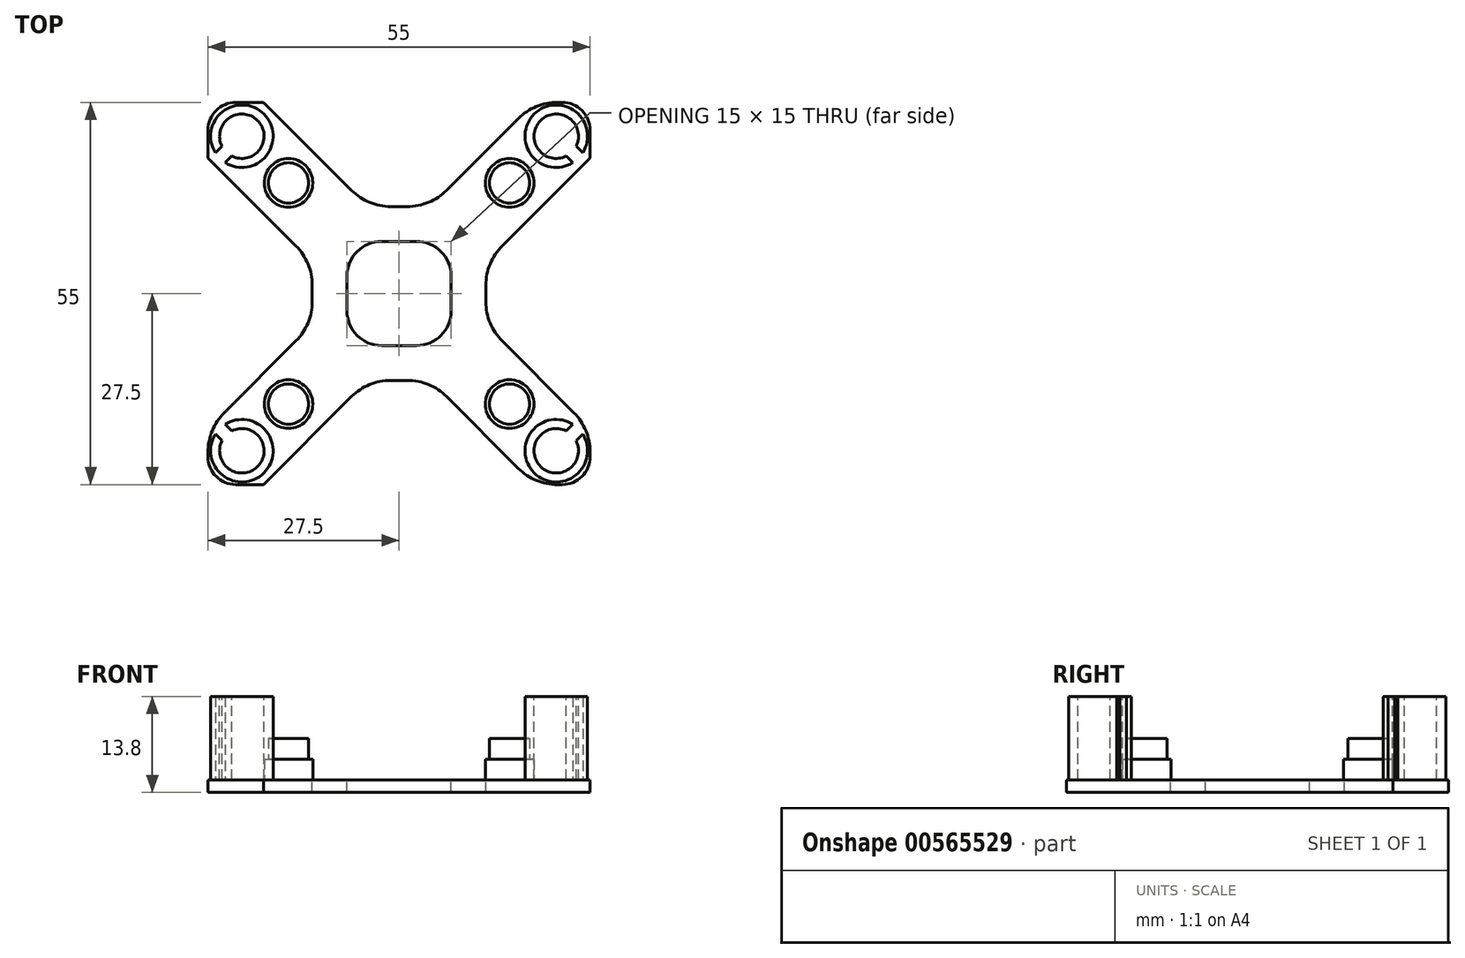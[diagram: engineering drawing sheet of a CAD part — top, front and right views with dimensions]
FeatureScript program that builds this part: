
annotation { "Feature Type Name" : "Feature", "Feature Type Description" : "" }
export const myFeature = defineFeature(function(context is Context, id is Id, definition is map)
    precondition{}
    {
        {
            var Q0;
            Q0=qCreatedBy(makeId("Top.planeOp"),FACE);
            var sketch = newSketch(context, id + "F0", { "sketchPlane" : qUnion([Q0])});
            skLineSegment(sketch, "E0.bottom", {"start": v(-27.5, 27.5) * mm, "end": v(27.5, 27.5) * mm});
            skLineSegment(sketch, "E0.top", {"start": v(-27.5, -27.5) * mm, "end": v(27.5, -27.5) * mm});
            skLineSegment(sketch, "E0.left", {"start": v(-27.5, 27.5) * mm, "end": v(-27.5, -27.5) * mm});
            skLineSegment(sketch, "E0.right", {"start": v(27.5, 27.5) * mm, "end": v(27.5, -27.5) * mm});
            skPoint(sketch, "E0.middle", {"position": v(0, 0) * mm});
            skLineSegment(sketch, "E1", {"start": v(-27.5, 27.5) * mm, "end": v(27.5, -27.5) * mm, "construction": true});
            skLineSegment(sketch, "E2", {"start": v(27.5, 27.5) * mm, "end": v(-27.5, -27.5) * mm, "construction": true});
            skSolve(sketch);
        }
        {
            var Q0;
            Q0=qSketchRegion(id+"F0",true);
            extrude(context, id + "F1", {"entities" : qUnion([Q0]), "depth" : 1.8 * mm, "offsetDistance" : 25 * mm});
        }
        {
            var Q0;
            Q0=makeQuery(id+"F1.opExtrude","CAP_FACE",FACE,{"disambiguationData":[OSD([sQuery(id+"F0.wireOp",EDGE,"E0.bottom"),sQuery(id+"F0.wireOp",EDGE,"E0.top"),sQuery(id+"F0.wireOp",EDGE,"E0.left"),sQuery(id+"F0.wireOp",EDGE,"E0.right")])],"isStart":false});
            var sketch = newSketch(context, id + "F2", { "sketchPlane" : qUnion([Q0])});
            skLineSegment(sketch, "E3", {"start": v(-27.5, 27.5) * mm, "end": v(27.5, -27.5) * mm, "construction": true});
            skLineSegment(sketch, "E4", {"start": v(27.5, 27.5) * mm, "end": v(-27.5, -27.5) * mm, "construction": true});
            skCircle(sketch, "E5", {"center": v(-15.9, 15.9) * mm, "radius": 3.5 * mm});
            skCircle(sketch, "E6", {"center": v(15.9, 15.9) * mm, "radius": 3.5 * mm});
            skCircle(sketch, "E7", {"center": v(-15.9, -15.9) * mm, "radius": 3.5 * mm});
            skCircle(sketch, "E8", {"center": v(15.9, -15.9) * mm, "radius": 3.5 * mm});
            skSolve(sketch);
        }
        {
            var Q0;
            Q0=qSketchRegion(id+"F2",true);
            extrude(context, id + "F3", {"entities" : qUnion([Q0]), "operationType" : NewBodyOperationType.ADD, "depth" : 3 * mm, "offsetDistance" : 25 * mm});
        }
        {
            var Q0;
            Q0=makeQuery(id+"F3.opExtrude","CAP_FACE",FACE,{"disambiguationData":[OSD([sQuery(id+"F2.wireOp",EDGE,"E5")])],"isStart":false});
            var sketch = newSketch(context, id + "F4", { "sketchPlane" : qUnion([Q0])});
            skCircle(sketch, "E9", {"center": v(-15.9, 15.9) * mm, "radius": 2.9 * mm});
            skCircle(sketch, "E10", {"center": v(15.9, 15.9) * mm, "radius": 2.9 * mm});
            skCircle(sketch, "E11", {"center": v(-15.9, -15.9) * mm, "radius": 2.9 * mm});
            skCircle(sketch, "E12", {"center": v(15.9, -15.9) * mm, "radius": 2.9 * mm});
            skSolve(sketch);
        }
        {
            var Q0;
            Q0=qSketchRegion(id+"F4",true);
            extrude(context, id + "F5", {"entities" : qUnion([Q0]), "operationType" : NewBodyOperationType.ADD, "depth" : 3 * mm, "offsetDistance" : 25 * mm});
        }
        {
            var Q0;
            Q0=makeQuery(id+"F1.opExtrude","CAP_FACE",FACE,{"disambiguationData":[OSD([sQuery(id+"F0.wireOp",EDGE,"E0.bottom"),sQuery(id+"F0.wireOp",EDGE,"E0.top"),sQuery(id+"F0.wireOp",EDGE,"E0.left"),sQuery(id+"F0.wireOp",EDGE,"E0.right")])],"isStart":false});
            var sketch = newSketch(context, id + "F6", { "sketchPlane" : qUnion([Q0])});
            skLineSegment(sketch, "E13", {"start": v(-27.5, 27.5) * mm, "end": v(27.5, -27.5) * mm, "construction": true});
            skLineSegment(sketch, "E14", {"start": v(27.5, 27.5) * mm, "end": v(-27.5, -27.5) * mm, "construction": true});
            skCircle(sketch, "E15", {"center": v(-22.63, 22.63) * mm, "radius": 4.5 * mm});
            skCircle(sketch, "E16", {"center": v(22.63, 22.63) * mm, "radius": 4.5 * mm});
            skCircle(sketch, "E17", {"center": v(22.63, -22.63) * mm, "radius": 4.5 * mm});
            skCircle(sketch, "E18", {"center": v(-22.63, -22.63) * mm, "radius": 4.5 * mm});
            skSolve(sketch);
        }
        {
            var Q0;
            Q0=qSketchRegion(id+"F6",true);
            extrude(context, id + "F7", {"entities" : qUnion([Q0]), "operationType" : NewBodyOperationType.ADD, "depth" : 12 * mm, "offsetDistance" : 25 * mm});
        }
        {
            var Q0;
            Q0=makeQuery(id+"F7.opExtrude","CAP_FACE",FACE,{"disambiguationData":[OSD([sQuery(id+"F6.wireOp",EDGE,"E18")])],"isStart":false});
            var sketch = newSketch(context, id + "F8", { "sketchPlane" : qUnion([Q0])});
            skCircle(sketch, "E19", {"center": v(-22.63, -22.63) * mm, "radius": 3.2 * mm});
            skCircle(sketch, "E20", {"center": v(22.63, -22.63) * mm, "radius": 3.2 * mm});
            skCircle(sketch, "E21", {"center": v(-22.63, 22.63) * mm, "radius": 3.2 * mm});
            skCircle(sketch, "E22", {"center": v(22.63, 22.63) * mm, "radius": 3.2 * mm});
            skSolve(sketch);
        }
        {
            var Q0;
            Q0=qSketchRegion(id+"F8",true);
            extrude(context, id + "F9", {"entities" : qUnion([Q0]), "operationType" : NewBodyOperationType.REMOVE, "oppositeDirection" : true, "depth" : 12 * mm, "offsetDistance" : 25 * mm});
        }
        {
            var Q0;
            Q0=makeQuery(id+"F1.opExtrude","SWEPT_EDGE",EDGE,{"disambiguationData":[OSD([sQuery(id+"F0.wireOp",EDGE,"E0.top"),sQuery(id+"F0.wireOp",EDGE,"E0.right")])]});
            var Q1;
            Q1=makeQuery(id+"F1.opExtrude","SWEPT_EDGE",EDGE,{"disambiguationData":[OSD([sQuery(id+"F0.wireOp",EDGE,"E0.top"),sQuery(id+"F0.wireOp",EDGE,"E0.left")])]});
            var Q2;
            Q2=makeQuery(id+"F1.opExtrude","SWEPT_EDGE",EDGE,{"disambiguationData":[OSD([sQuery(id+"F0.wireOp",EDGE,"E0.bottom"),sQuery(id+"F0.wireOp",EDGE,"E0.left")])]});
            var Q3;
            Q3=makeQuery(id+"F1.opExtrude","SWEPT_EDGE",EDGE,{"disambiguationData":[OSD([sQuery(id+"F0.wireOp",EDGE,"E0.bottom"),sQuery(id+"F0.wireOp",EDGE,"E0.right")])]});
            fillet(context, id + "F10", {"entities" : qUnion([Q0, Q1, Q2, Q3]), "radius" : 4 * mm, "tangentPropagation" : true, "allowEdgeOverflow" : false});
        }
        {
            var Q0;
            Q0=makeQuery(id+"F1.opExtrude","CAP_FACE",FACE,{"disambiguationData":[OSD([sQuery(id+"F0.wireOp",EDGE,"E0.bottom"),sQuery(id+"F0.wireOp",EDGE,"E0.top"),sQuery(id+"F0.wireOp",EDGE,"E0.left"),sQuery(id+"F0.wireOp",EDGE,"E0.right")])],"isStart":false});
            var sketch = newSketch(context, id + "F11", { "sketchPlane" : qUnion([Q0])});
            skLineSegment(sketch, "E23.0", {"start": v(-27.5, 27.5) * mm, "end": v(27.5, -27.5) * mm, "construction": true});
            skLineSegment(sketch, "E24.0", {"start": v(27.5, 27.5) * mm, "end": v(-27.5, -27.5) * mm, "construction": true});
            skPoint(sketch, "E25.middle", {"position": v(0, 0) * mm});
            skLineSegment(sketch, "E26", {"start": v(-12.5, 12.5) * mm, "end": v(12.5, 12.5) * mm, "construction": true});
            skLineSegment(sketch, "E27", {"start": v(-12.5, 12.5) * mm, "end": v(-12.5, -12.5) * mm, "construction": true});
            skLineSegment(sketch, "E28", {"start": v(-12.5, -12.5) * mm, "end": v(12.5, -12.5) * mm, "construction": true});
            skLineSegment(sketch, "E29", {"start": v(12.5, -12.5) * mm, "end": v(12.5, 12.5) * mm, "construction": true});
            skLineSegment(sketch, "E30", {"start": v(-27.5, 19.5) * mm, "end": v(-12.5, 4.5) * mm});
            skLineSegment(sketch, "E31", {"start": v(-12.5, 4.5) * mm, "end": v(-12.5, -4.5) * mm});
            skLineSegment(sketch, "E32", {"start": v(-12.5, -4.5) * mm, "end": v(-27.5, -19.5) * mm});
            skLineSegment(sketch, "E33", {"start": v(-27.5, -19.5) * mm, "end": v(-27.5, 19.5) * mm});
            skLineSegment(sketch, "E34", {"start": v(-19.5, 27.5) * mm, "end": v(-4.5, 12.5) * mm});
            skLineSegment(sketch, "E35", {"start": v(-4.5, 12.5) * mm, "end": v(4.5, 12.5) * mm});
            skLineSegment(sketch, "E36", {"start": v(4.5, 12.5) * mm, "end": v(19.5, 27.5) * mm});
            skLineSegment(sketch, "E37", {"start": v(19.5, 27.5) * mm, "end": v(-19.5, 27.5) * mm});
            skLineSegment(sketch, "E38", {"start": v(27.5, 19.5) * mm, "end": v(12.5, 4.5) * mm});
            skLineSegment(sketch, "E39", {"start": v(12.5, 4.5) * mm, "end": v(12.5, -4.5) * mm});
            skLineSegment(sketch, "E40", {"start": v(12.5, -4.5) * mm, "end": v(27.5, -19.5) * mm});
            skLineSegment(sketch, "E41", {"start": v(27.5, -19.5) * mm, "end": v(27.5, 19.5) * mm});
            skLineSegment(sketch, "E42", {"start": v(-19.5, -27.5) * mm, "end": v(-4.5, -12.5) * mm});
            skLineSegment(sketch, "E43", {"start": v(-4.5, -12.5) * mm, "end": v(4.5, -12.5) * mm});
            skLineSegment(sketch, "E44", {"start": v(4.5, -12.5) * mm, "end": v(19.5, -27.5) * mm});
            skLineSegment(sketch, "E45", {"start": v(19.5, -27.5) * mm, "end": v(-19.5, -27.5) * mm});
            skLineSegment(sketch, "E46.bottom", {"start": v(7.5, -7.5) * mm, "end": v(-7.5, -7.5) * mm});
            skLineSegment(sketch, "E46.top", {"start": v(7.5, 7.5) * mm, "end": v(-7.5, 7.5) * mm});
            skLineSegment(sketch, "E46.left", {"start": v(7.5, -7.5) * mm, "end": v(7.5, 7.5) * mm});
            skLineSegment(sketch, "E46.right", {"start": v(-7.5, -7.5) * mm, "end": v(-7.5, 7.5) * mm});
            skSolve(sketch);
        }
        {
            var Q0;
            Q0=qSketchRegion(id+"F11",true);
            extrude(context, id + "F12", {"entities" : qUnion([Q0]), "operationType" : NewBodyOperationType.REMOVE, "endBound" : BoundingType.SYMMETRIC, "oppositeDirection" : true, "depth" : 40 * mm, "offsetDistance" : 25 * mm});
        }
        {
            var Q0;
            Q0=makeQuery(id+"F1.opExtrude","CAP_FACE",FACE,{"disambiguationData":[OSD([sQuery(id+"F0.wireOp",EDGE,"E0.bottom"),sQuery(id+"F0.wireOp",EDGE,"E0.top"),sQuery(id+"F0.wireOp",EDGE,"E0.left"),sQuery(id+"F0.wireOp",EDGE,"E0.right")])],"isStart":false});
            var sketch = newSketch(context, id + "F13", { "sketchPlane" : qUnion([Q0])});
            skLineSegment(sketch, "E47", {"start": v(-14.9, 30.35) * mm, "end": v(-30.28, 14.98) * mm, "construction": true});
            skLineSegment(sketch, "E48", {"start": v(-22.63, 22.63) * mm, "end": v(22.63, 22.63) * mm, "construction": true});
            skPoint(sketch, "E49.cornerSnap0", {"position": v(-27.5, 21.5) * mm});
            skLineSegment(sketch, "E50", {"start": v(-25.43, 18.4) * mm, "end": v(-22.6, 21.24) * mm});
            skLineSegment(sketch, "E51", {"start": v(-22.6, 21.24) * mm, "end": v(-24.02, 22.65) * mm});
            skLineSegment(sketch, "E52", {"start": v(-24.02, 22.65) * mm, "end": v(-26.85, 19.82) * mm});
            skLineSegment(sketch, "E53", {"start": v(-26.85, 19.82) * mm, "end": v(-25.43, 18.4) * mm});
            skLineSegment(sketch, "E54.MirrorCS", {"start": v(25.43, 18.4) * mm, "end": v(22.6, 21.24) * mm});
            skLineSegment(sketch, "E55.MirrorCS", {"start": v(26.85, 19.82) * mm, "end": v(25.43, 18.4) * mm});
            skLineSegment(sketch, "E56.MirrorCS", {"start": v(22.6, 21.24) * mm, "end": v(24.02, 22.65) * mm});
            skLineSegment(sketch, "E57.MirrorCS", {"start": v(24.02, 22.65) * mm, "end": v(26.85, 19.82) * mm});
            skLineSegment(sketch, "E58.MirrorCS", {"start": v(-26.85, -19.82) * mm, "end": v(-25.43, -18.4) * mm});
            skLineSegment(sketch, "E59.MirrorCS", {"start": v(-24.02, -22.65) * mm, "end": v(-26.85, -19.82) * mm});
            skLineSegment(sketch, "E60.MirrorCS", {"start": v(-22.6, -21.24) * mm, "end": v(-24.02, -22.65) * mm});
            skLineSegment(sketch, "E61.MirrorCS", {"start": v(-25.43, -18.4) * mm, "end": v(-22.6, -21.24) * mm});
            skLineSegment(sketch, "E62.MirrorCS", {"start": v(25.43, -18.4) * mm, "end": v(22.6, -21.24) * mm});
            skLineSegment(sketch, "E63.MirrorCS", {"start": v(24.02, -22.65) * mm, "end": v(26.85, -19.82) * mm});
            skLineSegment(sketch, "E64.MirrorCS", {"start": v(26.85, -19.82) * mm, "end": v(25.43, -18.4) * mm});
            skLineSegment(sketch, "E65.MirrorCS", {"start": v(22.6, -21.24) * mm, "end": v(24.02, -22.65) * mm});
            skSolve(sketch);
        }
        {
            var Q0;
            Q0=qSketchRegion(id+"F13",true);
            extrude(context, id + "F14", {"entities" : qUnion([Q0]), "operationType" : NewBodyOperationType.REMOVE, "depth" : 25 * mm, "offsetDistance" : 25 * mm});
        }
        {
            var Q0;
            Q0=makeQuery(id+"F12.boolean.opBoolean","COPY",EDGE,{"derivedFrom":makeQuery(id+"F12.opExtrude","SWEPT_EDGE",EDGE,{"disambiguationData":[OSD([sQuery(id+"F0.wireOp",EDGE,"E0.top"),sQuery(id+"F11.wireOp",EDGE,"E44"),sQuery(id+"F11.wireOp",EDGE,"E45")])]})});
            var Q1;
            Q1=makeQuery(id+"F12.boolean.opBoolean","COPY",EDGE,{"derivedFrom":makeQuery(id+"F12.opExtrude","SWEPT_EDGE",EDGE,{"disambiguationData":[OSD([sQuery(id+"F11.wireOp",EDGE,"E43"),sQuery(id+"F11.wireOp",EDGE,"E44")])]})});
            var Q2;
            Q2=makeQuery(id+"F12.boolean.opBoolean","COPY",EDGE,{"derivedFrom":makeQuery(id+"F12.opExtrude","SWEPT_EDGE",EDGE,{"disambiguationData":[OSD([sQuery(id+"F11.wireOp",EDGE,"E42"),sQuery(id+"F11.wireOp",EDGE,"E43")])]})});
            var Q3;
            Q3=makeQuery(id+"F12.boolean.opBoolean","COPY",EDGE,{"derivedFrom":makeQuery(id+"F12.opExtrude","SWEPT_EDGE",EDGE,{"disambiguationData":[OSD([sQuery(id+"F0.wireOp",EDGE,"E0.top"),sQuery(id+"F11.wireOp",EDGE,"E42"),sQuery(id+"F11.wireOp",EDGE,"E45")])]})});
            var Q4;
            Q4=makeQuery(id+"F12.boolean.opBoolean","COPY",EDGE,{"derivedFrom":makeQuery(id+"F12.opExtrude","SWEPT_EDGE",EDGE,{"disambiguationData":[OSD([sQuery(id+"F0.wireOp",EDGE,"E0.left"),sQuery(id+"F11.wireOp",EDGE,"E32"),sQuery(id+"F11.wireOp",EDGE,"E33")])]})});
            var Q5;
            Q5=makeQuery(id+"F12.boolean.opBoolean","COPY",EDGE,{"derivedFrom":makeQuery(id+"F12.opExtrude","SWEPT_EDGE",EDGE,{"disambiguationData":[OSD([sQuery(id+"F11.wireOp",EDGE,"E31"),sQuery(id+"F11.wireOp",EDGE,"E32")])]})});
            var Q6;
            Q6=makeQuery(id+"F12.boolean.opBoolean","COPY",EDGE,{"derivedFrom":makeQuery(id+"F12.opExtrude","SWEPT_EDGE",EDGE,{"disambiguationData":[OSD([sQuery(id+"F11.wireOp",EDGE,"E30"),sQuery(id+"F11.wireOp",EDGE,"E31")])]})});
            var Q7;
            Q7=makeQuery(id+"F12.boolean.opBoolean","COPY",EDGE,{"derivedFrom":makeQuery(id+"F12.opExtrude","SWEPT_EDGE",EDGE,{"disambiguationData":[OSD([sQuery(id+"F0.wireOp",EDGE,"E0.left"),sQuery(id+"F11.wireOp",EDGE,"E30"),sQuery(id+"F11.wireOp",EDGE,"E33")])]})});
            var Q8;
            Q8=makeQuery(id+"F12.boolean.opBoolean","COPY",EDGE,{"derivedFrom":makeQuery(id+"F12.opExtrude","SWEPT_EDGE",EDGE,{"disambiguationData":[OSD([sQuery(id+"F0.wireOp",EDGE,"E0.bottom"),sQuery(id+"F11.wireOp",EDGE,"E34"),sQuery(id+"F11.wireOp",EDGE,"E37")])]})});
            var Q9;
            Q9=makeQuery(id+"F12.boolean.opBoolean","COPY",EDGE,{"derivedFrom":makeQuery(id+"F12.opExtrude","SWEPT_EDGE",EDGE,{"disambiguationData":[OSD([sQuery(id+"F11.wireOp",EDGE,"E34"),sQuery(id+"F11.wireOp",EDGE,"E35")])]})});
            var Q10;
            Q10=makeQuery(id+"F12.boolean.opBoolean","COPY",EDGE,{"derivedFrom":makeQuery(id+"F12.opExtrude","SWEPT_EDGE",EDGE,{"disambiguationData":[OSD([sQuery(id+"F11.wireOp",EDGE,"E35"),sQuery(id+"F11.wireOp",EDGE,"E36")])]})});
            var Q11;
            Q11=makeQuery(id+"F12.boolean.opBoolean","COPY",EDGE,{"derivedFrom":makeQuery(id+"F12.opExtrude","SWEPT_EDGE",EDGE,{"disambiguationData":[OSD([sQuery(id+"F0.wireOp",EDGE,"E0.bottom"),sQuery(id+"F11.wireOp",EDGE,"E36"),sQuery(id+"F11.wireOp",EDGE,"E37")])]})});
            var Q12;
            Q12=makeQuery(id+"F12.boolean.opBoolean","COPY",EDGE,{"derivedFrom":makeQuery(id+"F12.opExtrude","SWEPT_EDGE",EDGE,{"disambiguationData":[OSD([sQuery(id+"F11.wireOp",EDGE,"E39"),sQuery(id+"F11.wireOp",EDGE,"E40")])]})});
            var Q13;
            Q13=makeQuery(id+"F12.boolean.opBoolean","COPY",EDGE,{"derivedFrom":makeQuery(id+"F12.opExtrude","SWEPT_EDGE",EDGE,{"disambiguationData":[OSD([sQuery(id+"F11.wireOp",EDGE,"E38"),sQuery(id+"F11.wireOp",EDGE,"E39")])]})});
            var Q14;
            Q14=makeQuery(id+"F12.boolean.opBoolean","COPY",EDGE,{"derivedFrom":makeQuery(id+"F12.opExtrude","SWEPT_EDGE",EDGE,{"disambiguationData":[OSD([sQuery(id+"F0.wireOp",EDGE,"E0.right"),sQuery(id+"F11.wireOp",EDGE,"E38"),sQuery(id+"F11.wireOp",EDGE,"E41")])]})});
            var Q15;
            Q15=makeQuery(id+"F12.boolean.opBoolean","COPY",EDGE,{"derivedFrom":makeQuery(id+"F12.opExtrude","SWEPT_EDGE",EDGE,{"disambiguationData":[OSD([sQuery(id+"F0.wireOp",EDGE,"E0.right"),sQuery(id+"F11.wireOp",EDGE,"E40"),sQuery(id+"F11.wireOp",EDGE,"E41")])]})});
            fillet(context, id + "F15", {"entities" : qUnion([Q0, Q1, Q2, Q3, Q4, Q5, Q6, Q7, Q8, Q9, Q10, Q11, Q12, Q13, Q14, Q15]), "radius" : 8 * mm, "tangentPropagation" : true, "allowEdgeOverflow" : false});
        }
        {
            var Q0;
            Q0=makeQuery(id+"F12.boolean.opBoolean","COPY",EDGE,{"derivedFrom":makeQuery(id+"F12.opExtrude","SWEPT_EDGE",EDGE,{"disambiguationData":[OSD([sQuery(id+"F11.wireOp",EDGE,"E46.top"),sQuery(id+"F11.wireOp",EDGE,"E46.right")])]})});
            var Q1;
            Q1=makeQuery(id+"F12.boolean.opBoolean","COPY",EDGE,{"derivedFrom":makeQuery(id+"F12.opExtrude","SWEPT_EDGE",EDGE,{"disambiguationData":[OSD([sQuery(id+"F11.wireOp",EDGE,"E46.top"),sQuery(id+"F11.wireOp",EDGE,"E46.left")])]})});
            var Q2;
            Q2=makeQuery(id+"F12.boolean.opBoolean","COPY",EDGE,{"derivedFrom":makeQuery(id+"F12.opExtrude","SWEPT_EDGE",EDGE,{"disambiguationData":[OSD([sQuery(id+"F11.wireOp",EDGE,"E46.bottom"),sQuery(id+"F11.wireOp",EDGE,"E46.left")])]})});
            var Q3;
            Q3=makeQuery(id+"F12.boolean.opBoolean","COPY",EDGE,{"derivedFrom":makeQuery(id+"F12.opExtrude","SWEPT_EDGE",EDGE,{"disambiguationData":[OSD([sQuery(id+"F11.wireOp",EDGE,"E46.bottom"),sQuery(id+"F11.wireOp",EDGE,"E46.right")])]})});
            fillet(context, id + "F16", {"entities" : qUnion([Q0, Q1, Q2, Q3]), "radius" : 5 * mm, "tangentPropagation" : true, "allowEdgeOverflow" : false});
        }
    });
